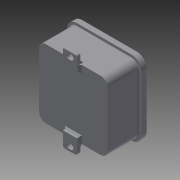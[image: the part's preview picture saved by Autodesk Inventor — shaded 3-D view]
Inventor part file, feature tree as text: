
AUTODESK INVENTOR PART (.ipt)
format: ipt  version: 2013 SP2 (Build 170200200, 200)  size: 223,744 bytes
history: native  units: mm
features: extrude x5, sketch x5, fillet x4, plane x3, mirror x2, chamfer x1, projected_geometry x1
ambient origin geometry x8: Origin, YZ Plane, XZ Plane, XY Plane, X Axis, Y Axis, Z Axis, Center Point
bodies: Solid1 (feature_tree)
feature tree (21):
  extrude  "Extrusion1"  Depth=69.0mm
  fillet  "Fillet1"  Radius=31.0mm
  extrude  "Extrusion2"  Depth=3.0mm
  fillet  "Fillet2"  Radius=6.0mm
  fillet  "Fillet3"  Radius=1.0mm
  extrude  "Extrusion3"  Depth=14.0mm
  chamfer  "Chamfer1"  Distance=3.5mm
  extrude  "Extrusion4"  Depth=1.5mm TaperAngle=45.0deg
  extrude  "Extrusion5"  Depth=1.0mm
  plane  "Work Plane1"
  mirror  "Mirror1"
  fillet  "Fillet4"  Radius=1.0mm
  plane  "Work Plane2"
  mirror  "Mirror2"
  sketch  "Sketch1"  dims[d0=69.0mm d1=69.0mm d2=31.0mm d3=0.0mm]
  sketch  "Sketch2"  dims[d4=7.0mm d5=3.0mm d6=6.0mm d7=0.0mm d8=1.0mm]
  sketch  "Sketch3"  dims[d9=1.0mm d10=14.0mm]
  sketch  "Sketch4"  dims[d12=15.0mm]
  sketch  "Sketch5"  dims[d13=9.0mm d14=3.5mm d15=0.0mm d16=1.5mm d17=2.0mm d18=45.0deg d19=1.0mm d20=1.0mm d21=5.0mm d22=5.0mm d23=3.5mm d24=0.0mm d25=45.0deg d26=3.0mm d27=1.5mm d28=0.0mm d29=1.5mm]
  projected_geometry  "Projected Loop1"
  plane  "Work Plane3"
